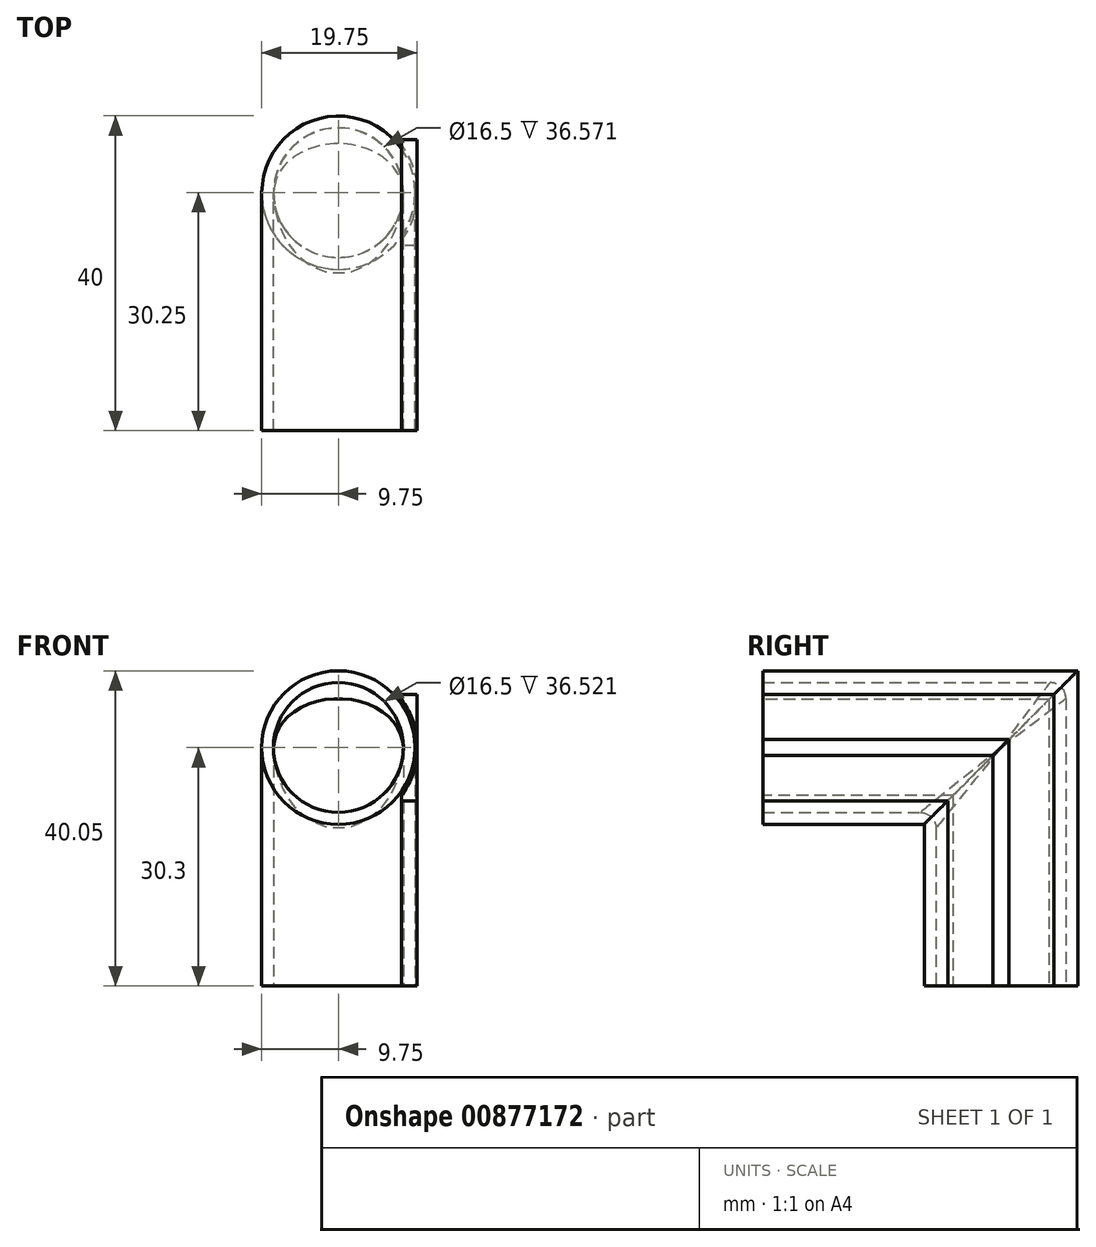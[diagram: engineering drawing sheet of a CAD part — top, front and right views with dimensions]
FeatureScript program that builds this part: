
annotation { "Feature Type Name" : "Feature", "Feature Type Description" : "" }
export const myFeature = defineFeature(function(context is Context, id is Id, definition is map)
    precondition{}
    {
        {
            var Q0;
            Q0=qCreatedBy(makeId("Front.planeOp"),FACE);
            var sketch = newSketch(context, id + "F0", { "sketchPlane" : qUnion([Q0])});
            skCircle(sketch, "E0", {"center": v(0, 0) * mm, "radius": 9.75 * mm});
            skCircle(sketch, "E1", {"center": v(0, 0) * mm, "radius": 8.25 * mm});
            skSolve(sketch);
        }
        {
            var Q0;
            Q0 = qSketchRegion(id + "F0", true);
            extrude(context, id + "F1", {"entities" : qUnion([Q0]), "depth" : 40 * mm, "offsetDistance" : 25 * mm});
        }
        {
            var Q0;
            Q0=qCreatedBy(makeId("Right.planeOp"),FACE);
            var sketch = newSketch(context, id + "F2", { "sketchPlane" : qUnion([Q0])});
            skLineSegment(sketch, "E2.0", {"start": v(0, -9.75) * mm, "end": v(0, 9.75) * mm});
            skLineSegment(sketch, "E3", {"start": v(0, 9.75) * mm, "end": v(-19.5, -9.75) * mm});
            skLineSegment(sketch, "E4", {"start": v(-19.5, -9.75) * mm, "end": v(0, -9.75) * mm});
            skLineSegment(sketch, "E5.0", {"start": v(-40, -9.75) * mm, "end": v(-40, 9.75) * mm});
            skLineSegment(sketch, "E6", {"start": v(-40, -9.75) * mm, "end": v(-19.5, -9.75) * mm, "construction": true});
            skSolve(sketch);
        }
        {
            var Q0;
            Q0 = qSketchRegion(id + "F2", true);
            extrude(context, id + "F3", {"entities" : qUnion([Q0]), "operationType" : NewBodyOperationType.REMOVE, "endBound" : BoundingType.SYMMETRIC, "oppositeDirection" : true, "depth" : 25 * mm, "offsetDistance" : 25 * mm});
        }
        {
            var Q0;
            Q0=qCreatedBy(makeId("Top.planeOp"),FACE);
            cPlane(context, id + "F4", {"entities" : qUnion([Q0]), "cplaneType" : CPlaneType.OFFSET, "offset" : 30.3 * mm, "oppositeDirection" : true, "width" : 150 * mm, "height" : 150 * mm});
        }
        {
            var Q0;
            Q0=qCreatedBy(id+"F4.planeOp",FACE);
            var sketch = newSketch(context, id + "F5", { "sketchPlane" : qUnion([Q0])});
            skCircle(sketch, "E7.0", {"center": v(0, -9.75) * mm, "radius": 8.25 * mm});
            skCircle(sketch, "E7.1", {"center": v(0, -9.75) * mm, "radius": 9.75 * mm});
            skSolve(sketch);
        }
        {
            var Q0;
            Q0 = qSketchRegion(id + "F5", true);
            var Q1;
            Q1=makeQuery(id+"F3.boolean.opBoolean","COPY",FACE,{"derivedFrom":makeQuery(id+"F3.opExtrude","SWEPT_FACE",FACE,{"disambiguationData":[OSD([sQuery(id+"F2.wireOp",EDGE,"E3")])]})});
            extrude(context, id + "F6", {"entities" : qUnion([Q0]), "operationType" : NewBodyOperationType.ADD, "endBound" : BoundingType.UP_TO_SURFACE, "depth" : 25 * mm, "endBoundEntityFace" : qUnion([Q1]), "offsetDistance" : 25 * mm});
        }
        {
            var Q0;
            Q0=qCreatedBy(makeId("Right.planeOp"),FACE);
            cPlane(context, id + "F7", {"entities" : qUnion([Q0]), "cplaneType" : CPlaneType.OFFSET, "offset" : 8 * mm, "width" : 150 * mm, "height" : 150 * mm});
        }
        {
            var Q0;
            Q0=qCreatedBy(id+"F7.planeOp",FACE);
            var sketch = newSketch(context, id + "F8", { "sketchPlane" : qUnion([Q0])});
            skLineSegment(sketch, "E8.top", {"start": v(-40, 6.75) * mm, "end": v(-3, 6.75) * mm});
            skLineSegment(sketch, "E8.left", {"start": v(-40, -6.75) * mm, "end": v(-40, 6.75) * mm});
            skLineSegment(sketch, "E9.top", {"start": v(-3, -30.3) * mm, "end": v(-16.5, -30.3) * mm});
            skLineSegment(sketch, "E9.right", {"start": v(-16.5, -6.75) * mm, "end": v(-16.5, -30.3) * mm});
            skLineSegment(sketch, "E10", {"start": v(-16.5, -6.75) * mm, "end": v(-40, -6.75) * mm});
            skLineSegment(sketch, "E11", {"start": v(-3, 6.75) * mm, "end": v(-3, -30.3) * mm});
            skLineSegment(sketch, "E12", {"start": v(-16.5, -30.3) * mm, "end": v(-19.5, -30.3) * mm, "construction": true});
            skLineSegment(sketch, "E13", {"start": v(-3, -30.3) * mm, "end": v(0, -30.3) * mm, "construction": true});
            skLineSegment(sketch, "E14.0", {"start": v(-19.5, -30.3) * mm, "end": v(0, -30.3) * mm});
            skSolve(sketch);
        }
        {
            var Q0;
            Q0 = qSketchRegion(id + "F8", true);
            extrude(context, id + "F9", {"entities" : qUnion([Q0]), "operationType" : NewBodyOperationType.ADD, "depth" : 2 * mm, "offsetDistance" : 25 * mm});
        }
        {
            var Q0;
            Q0=makeQuery(id+"F9.opExtrude","CAP_VERTEX",VERTEX,{"disambiguationData":[OSD([sQuery(id+"F8.wireOp",EDGE,"E8.top"),sQuery(id+"F8.wireOp",EDGE,"E11")])],"isStart":false});
            var Q1;
            Q1=makeQuery(id+"F9.opExtrude","CAP_VERTEX",VERTEX,{"disambiguationData":[OSD([sQuery(id+"F8.wireOp",EDGE,"E9.right"),sQuery(id+"F8.wireOp",EDGE,"E10")])],"isStart":false});
            var Q2;
            Q2=makeQuery(id+"F9.opExtrude","CAP_VERTEX",VERTEX,{"disambiguationData":[OSD([sQuery(id+"F8.wireOp",EDGE,"E9.right"),sQuery(id+"F8.wireOp",EDGE,"E10")])],"isStart":true});
            cPlane(context, id + "F10", {"entities" : qUnion([Q0, Q1, Q2]), "cplaneType" : CPlaneType.THREE_POINT, "offset" : 25 * mm, "width" : 150 * mm, "height" : 150 * mm});
        }
        {
            var Q0;
            Q0=makeQuery(id+"F9.boolean.opBoolean","MERGE",FACE,{"derivedFrom":[makeQuery(id+"F1.opExtrude","CAP_FACE",FACE,{"disambiguationData":[OSD([sQuery(id+"F0.wireOp",EDGE,"E0"),sQuery(id+"F0.wireOp",EDGE,"E1")])],"isStart":false}),makeQuery(id+"F9.opExtrude","SWEPT_FACE",FACE,{"disambiguationData":[OSD([sQuery(id+"F8.wireOp",EDGE,"E8.left")])]})]});
            var sketch = newSketch(context, id + "F11", { "sketchPlane" : qUnion([Q0])});
            skCircle(sketch, "E15", {"center": v(0, 0) * mm, "radius": 9.75 * mm});
            skCircle(sketch, "E16", {"center": v(0, 0) * mm, "radius": 10.05 * mm});
            skCircle(sketch, "E17", {"center": v(0, 0) * mm, "radius": 8.25 * mm});
            skSolve(sketch);
        }
        {
            var Q0;
            Q0 = qSketchRegion(id + "F11", true);
            var Q1;
            {var subQ1=sQuery(id+"F0.wireOp",EDGE,"E1");var subQ2=sQuery(id+"F8.wireOp",EDGE,"E8.left");var subQ3=makeQuery(id+"F9.boolean.opBoolean","SPLIT",EDGE,{"disambiguationData":[TD([makeQuery(id+"F1.opExtrude","SWEPT_FACE",FACE,{"disambiguationData":[OSD([subQ1])]})])],"derivedFrom":makeQuery(id+"F9.opExtrude","CAP_EDGE",EDGE,{"disambiguationData":[OSD([subQ2])],"isStart":true})});Q1=makeQuery(id+"F11.imprint","IMPRINT",FACE,{"disambiguationData":[TD([[makeQuery(id+"F11.imprint","IMPRINT",EDGE,{"derivedFrom":subQ3}),-1.0]])]});}
            var Q2;
            Q2=qCreatedBy(id+"F10.planeOp",FACE);
            extrude(context, id + "F12", {"entities" : qUnion([Q0, Q1]), "operationType" : NewBodyOperationType.REMOVE, "endBound" : BoundingType.UP_TO_SURFACE, "oppositeDirection" : true, "depth" : 25 * mm, "endBoundEntityFace" : qUnion([Q2]), "offsetDistance" : 25 * mm});
        }
        {
            var Q0;
            Q0=makeQuery(id+"F9.boolean.opBoolean","MERGE",FACE,{"derivedFrom":[makeQuery(id+"F6.opExtrude","CAP_FACE",FACE,{"disambiguationData":[OSD([sQuery(id+"F5.wireOp",EDGE,"E7.0"),sQuery(id+"F5.wireOp",EDGE,"E7.1")])],"isStart":true}),makeQuery(id+"F9.opExtrude","SWEPT_FACE",FACE,{"disambiguationData":[OSD([sQuery(id+"F8.wireOp",EDGE,"E9.top")])]})]});
            var sketch = newSketch(context, id + "F13", { "sketchPlane" : qUnion([Q0])});
            skCircle(sketch, "E18", {"center": v(0, 9.75) * mm, "radius": 9.75 * mm});
            skCircle(sketch, "E19", {"center": v(0, 9.75) * mm, "radius": 10.05 * mm});
            skCircle(sketch, "E20", {"center": v(0, 9.75) * mm, "radius": 8.25 * mm});
            skSolve(sketch);
        }
        {
            var Q0;
            Q0 = qSketchRegion(id + "F13", true);
            var Q1;
            Q1=makeQuery(id+"F13.imprint","IMPRINT",FACE,{"disambiguationData":[TD([[makeQuery(id+"F13.imprint","IMPRINT",EDGE,{"disambiguationData":[OD(1.0)],"derivedFrom":sQuery(id+"F13.wireOp",EDGE,"E20")}),1.0]])]});
            var Q2;
            Q2=qCreatedBy(id+"F10.planeOp",FACE);
            extrude(context, id + "F14", {"entities" : qUnion([Q0, Q1]), "operationType" : NewBodyOperationType.REMOVE, "endBound" : BoundingType.UP_TO_SURFACE, "oppositeDirection" : true, "depth" : 25 * mm, "endBoundEntityFace" : qUnion([Q2]), "offsetDistance" : 25 * mm});
        }
        {
            var Q0;
            Q0=makeQuery(id+"F6.boolean.opBoolean","MERGE",EDGE,{"derivedFrom":[makeQuery(id+"F3.boolean.opBoolean","INTERSECT",EDGE,{"derivedFrom":[makeQuery(id+"F1.opExtrude","SWEPT_FACE",FACE,{"disambiguationData":[OSD([sQuery(id+"F0.wireOp",EDGE,"E1")])]}),makeQuery(id+"F3.opExtrude","SWEPT_FACE",FACE,{"disambiguationData":[OSD([sQuery(id+"F2.wireOp",EDGE,"E3")])]})]}),makeQuery(id+"F6.opExtrude","CAP_EDGE",EDGE,{"disambiguationData":[OSD([sQuery(id+"F5.wireOp",EDGE,"E7.0")])],"isStart":false})]});
            fillet(context, id + "F15", {"entities" : qUnion([Q0]), "tangentPropagation" : true, "radius" : 2 * mm, "defaultsChanged" : true, "vertexSettings" : [], "allowEdgeOverflow" : false});
        }
    });
